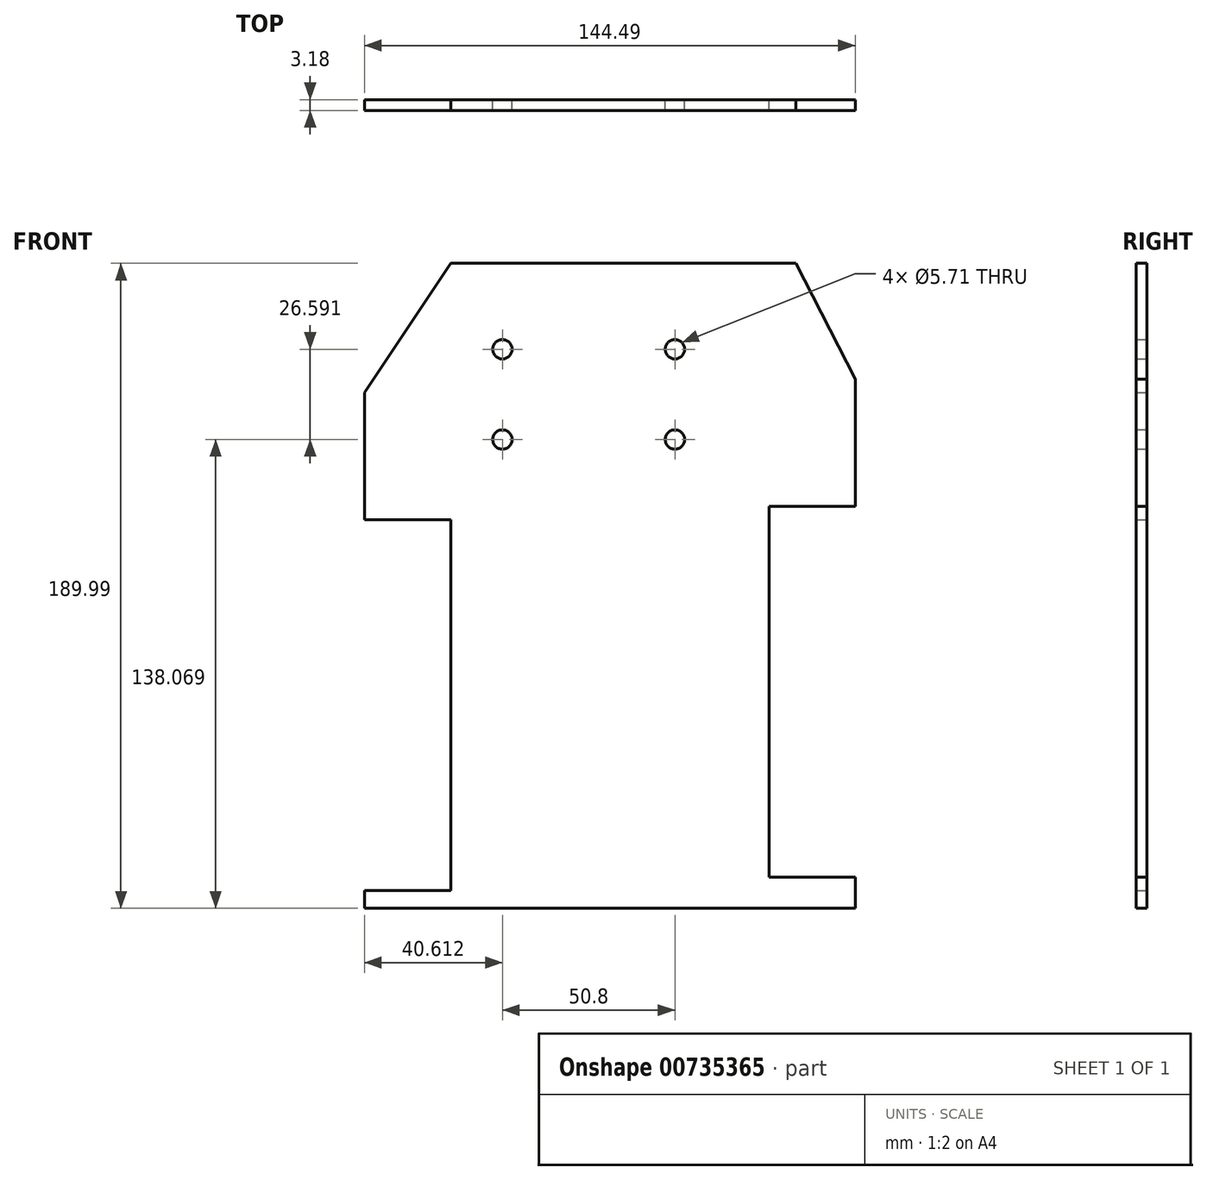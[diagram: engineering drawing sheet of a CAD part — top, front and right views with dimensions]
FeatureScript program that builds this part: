
annotation { "Feature Type Name" : "Feature", "Feature Type Description" : "" }
export const myFeature = defineFeature(function(context is Context, id is Id, definition is map)
    precondition{}
    {
        {
            var Q0;
            Q0=qCreatedBy(makeId("Front.planeOp"),FACE);
            var sketch = newSketch(context, id + "F0", { "sketchPlane" : qUnion([Q0])});
            skLineSegment(sketch, "E0.bottom", {"start": v(-134.92, 75.5) * mm, "end": v(-33.32, 75.5) * mm});
            skLineSegment(sketch, "E0.top", {"start": v(-160.32, -114.48) * mm, "end": v(-15.83, -114.48) * mm});
            skLineSegment(sketch, "E0.left", {"start": v(-160.32, 37.4) * mm, "end": v(-160.32, 0) * mm});
            skLineSegment(sketch, "E0.right", {"start": v(-15.83, 41.34) * mm, "end": v(-15.83, 3.93) * mm});
            skLineSegment(sketch, "E1", {"start": v(-160.32, -114.48) * mm, "end": v(-160.32, -109.22) * mm});
            skLineSegment(sketch, "E2", {"start": v(-15.83, -114.48) * mm, "end": v(-15.83, -105.29) * mm});
            skLineSegment(sketch, "E3", {"start": v(-160.32, 37.4) * mm, "end": v(-134.92, 75.5) * mm});
            skLineSegment(sketch, "E4", {"start": v(-33.32, 75.5) * mm, "end": v(-15.83, 41.34) * mm});
            skLineSegment(sketch, "E5.bottom", {"start": v(-160.32, 0) * mm, "end": v(-134.92, 0) * mm});
            skLineSegment(sketch, "E5.top", {"start": v(-160.32, -109.22) * mm, "end": v(-134.92, -109.22) * mm});
            skLineSegment(sketch, "E5.right", {"start": v(-134.92, 0) * mm, "end": v(-134.92, -109.22) * mm});
            skLineSegment(sketch, "E6.bottom", {"start": v(-15.83, 3.93) * mm, "end": v(-41.23, 3.93) * mm});
            skLineSegment(sketch, "E6.top", {"start": v(-15.83, -105.29) * mm, "end": v(-41.23, -105.29) * mm});
            skLineSegment(sketch, "E6.right", {"start": v(-41.23, 3.93) * mm, "end": v(-41.23, -105.29) * mm});
            skLineSegment(sketch, "E7.trimOffspring", {"start": v(-160.32, 0) * mm, "end": v(-160.32, 37.4) * mm});
            skLineSegment(sketch, "E8.trimOffspring", {"start": v(-160.32, -109.22) * mm, "end": v(-160.32, -114.48) * mm});
            skLineSegment(sketch, "E9.trimOffspring", {"start": v(-15.83, 3.93) * mm, "end": v(-15.83, 41.34) * mm});
            skLineSegment(sketch, "E10.trimOffspring", {"start": v(-15.83, -105.29) * mm, "end": v(-15.83, -114.48) * mm});
            skCircle(sketch, "E11", {"center": v(-119.7, 50.18) * mm, "radius": 2.86 * mm});
            skCircle(sketch, "E12", {"center": v(-119.7, 23.59) * mm, "radius": 2.86 * mm});
            skCircle(sketch, "E13", {"center": v(-68.9, 50.18) * mm, "radius": 2.86 * mm});
            skCircle(sketch, "E14", {"center": v(-68.9, 23.59) * mm, "radius": 2.86 * mm});
            skSolve(sketch);
        }
        {
            var Q0;
            Q0=makeQuery(id+"F0.imprint","IMPRINT",FACE,{"disambiguationData":[TD([[makeQuery(id+"F0.imprint","IMPRINT",EDGE,{"derivedFrom":sQuery(id+"F0.wireOp",EDGE,"E0.bottom")}),-1.0]])]});
            extrude(context, id + "F1", {"entities" : qUnion([Q0]), "depth" : 3.17 * mm, "offsetDistance" : 25.4 * mm});
        }
    });
